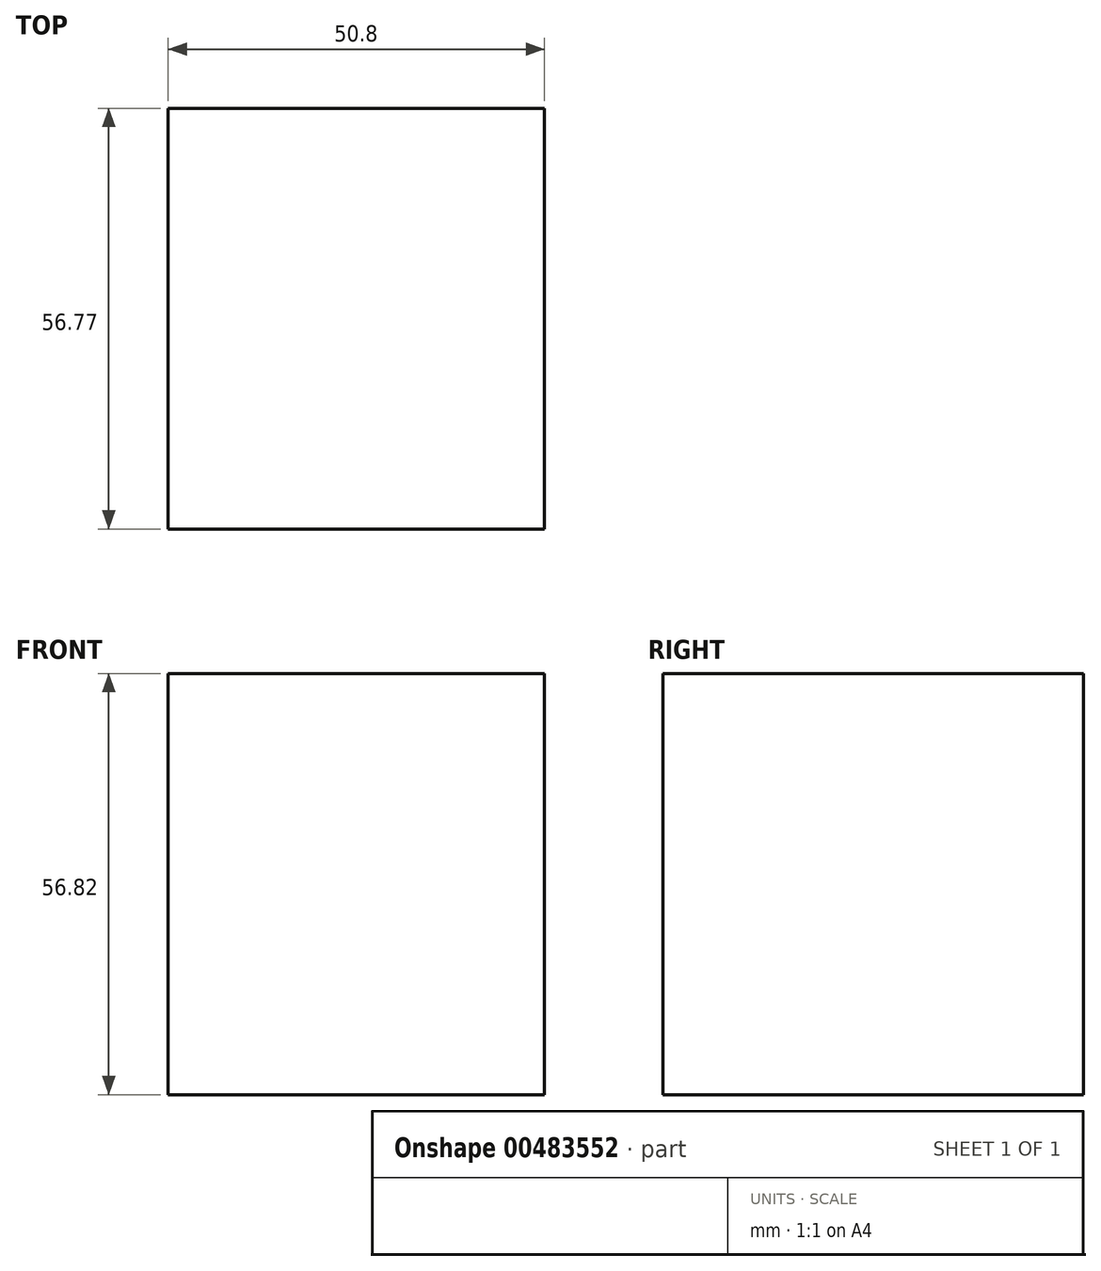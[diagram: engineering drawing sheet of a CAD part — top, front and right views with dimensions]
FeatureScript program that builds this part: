
annotation { "Feature Type Name" : "Feature", "Feature Type Description" : "" }
export const myFeature = defineFeature(function(context is Context, id is Id, definition is map)
    precondition{}
    {
        {
            var Q0;
            Q0=qCreatedBy(makeId("Right.planeOp"),FACE);
            var sketch = newSketch(context, id + "F0", { "sketchPlane" : qUnion([Q0])});
            skLineSegment(sketch, "E0.bottom", {"start": v(0, 0) * mm, "end": v(56.77, 0) * mm});
            skLineSegment(sketch, "E0.top", {"start": v(0, 56.82) * mm, "end": v(56.77, 56.82) * mm});
            skLineSegment(sketch, "E0.left", {"start": v(0, 0) * mm, "end": v(0, 56.82) * mm});
            skLineSegment(sketch, "E0.right", {"start": v(56.77, 0) * mm, "end": v(56.77, 56.82) * mm});
            skSolve(sketch);
        }
        {
            var Q0;
            Q0=makeQuery(id+"F0.imprint","IMPRINT",FACE,{"disambiguationData":[TD([[makeQuery(id+"F0.imprint","IMPRINT",EDGE,{"derivedFrom":sQuery(id+"F0.wireOp",EDGE,"E0.bottom")}),1.0]])]});
            extrude(context, id + "F1", {"entities" : qUnion([Q0]), "depth" : 50.8 * mm});
        }
    });
